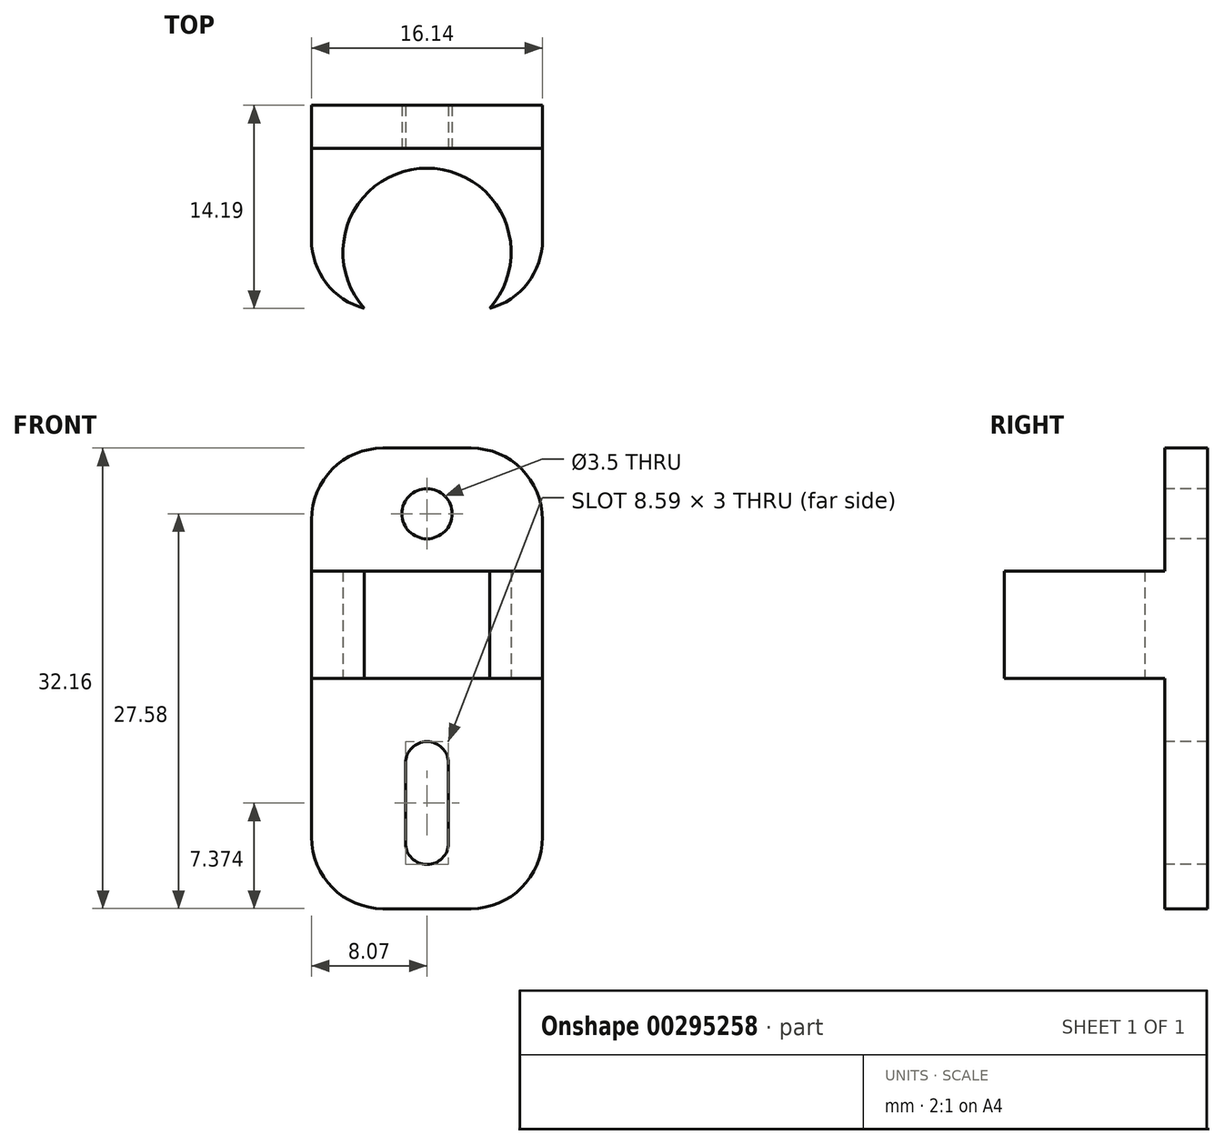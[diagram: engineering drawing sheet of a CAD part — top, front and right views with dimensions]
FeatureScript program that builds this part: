
annotation { "Feature Type Name" : "Feature", "Feature Type Description" : "" }
export const myFeature = defineFeature(function(context is Context, id is Id, definition is map)
    precondition{}
    {
        {
            var Q0;
            Q0=qCreatedBy(makeId("Top.planeOp"),FACE);
            var sketch = newSketch(context, id + "F0", { "sketchPlane" : qUnion([Q0])});
            skArc(sketch, "E0", {"start": v(4.37, -3.93) * mm, "mid": v(0, 5.88) * mm, "end": v(-4.37, -3.93) * mm});
            skLineSegment(sketch, "E1.bottom", {"start": v(8.07, 7.26) * mm, "end": v(-8.07, 7.26) * mm});
            skLineSegment(sketch, "E1.left", {"start": v(8.07, 7.26) * mm, "end": v(8.07, -7.26) * mm});
            skLineSegment(sketch, "E1.right", {"start": v(-8.07, 7.26) * mm, "end": v(-8.07, -7.26) * mm});
            skLineSegment(sketch, "E2", {"start": v(-4.37, -3.93) * mm, "end": v(-8.07, -7.26) * mm});
            skLineSegment(sketch, "E3", {"start": v(4.37, -3.93) * mm, "end": v(8.07, -7.26) * mm});
            skSolve(sketch);
        }
        {
            var Q0;
            Q0 = qSketchRegion(id + "F0", true);
            extrude(context, id + "F1", {"entities" : qUnion([Q0]), "depth" : 7.5 * mm});
        }
        {
            var Q0;
            Q0=makeQuery(id+"F1.opExtrude","SWEPT_FACE",FACE,{"disambiguationData":[OSD([sQuery(id+"F0.wireOp",EDGE,"E1.bottom")])]});
            var sketch = newSketch(context, id + "F2", { "sketchPlane" : qUnion([Q0])});
            skLineSegment(sketch, "E4.bottom", {"start": v(8.07, 0) * mm, "end": v(-8.07, 0) * mm});
            skLineSegment(sketch, "E4.top", {"start": v(8.07, 16.08) * mm, "end": v(-8.07, 16.08) * mm});
            skLineSegment(sketch, "E4.left", {"start": v(8.07, 0) * mm, "end": v(8.07, 16.08) * mm});
            skLineSegment(sketch, "E4.right", {"start": v(-8.07, 0) * mm, "end": v(-8.07, 16.08) * mm});
            skPoint(sketch, "E5", {"position": v(0, 11.5) * mm});
            skPoint(sketch, "E6.MirrorP", {"position": v(0, -11.5) * mm});
            skLineSegment(sketch, "E7.MirrorCS", {"start": v(-8.07, 0) * mm, "end": v(-8.07, -16.08) * mm});
            skLineSegment(sketch, "E8.MirrorCS", {"start": v(8.07, -16.08) * mm, "end": v(-8.07, -16.08) * mm});
            skLineSegment(sketch, "E9.MirrorCS", {"start": v(8.07, 0) * mm, "end": v(8.07, -16.08) * mm});
            skLineSegment(sketch, "E10", {"start": v(0, -11.5) * mm, "end": v(0, -5.91) * mm});
            skArc(sketch, "E11.0.startCap", {"start": v(1.5, -11.5) * mm, "mid": v(0, -13) * mm, "end": v(-1.5, -11.5) * mm});
            skArc(sketch, "E11.0.endCap", {"start": v(-1.5, -5.91) * mm, "mid": v(0, -4.41) * mm, "end": v(1.5, -5.91) * mm});
            skLineSegment(sketch, "E11.0.left", {"start": v(-1.5, -11.5) * mm, "end": v(-1.5, -5.91) * mm});
            skLineSegment(sketch, "E11.0.right", {"start": v(1.5, -11.5) * mm, "end": v(1.5, -5.91) * mm});
            skSolve(sketch);
        }
        {
            var Q0;
            Q0 = qSketchRegion(id + "F2", true);
            extrude(context, id + "F3", {"entities" : qUnion([Q0]), "operationType" : NewBodyOperationType.ADD, "depth" : 3 * mm});
        }
        {
            var Q0;
            Q0=sQuery(id+"F2.wireOp",VERTEX,"E5");
            var Q1;
            Q1=makeQuery(id+"F1.opExtrude","SWEPT_BODY",BODY,{"disambiguationData":[OSD([sQuery(id+"F0.wireOp",EDGE,"E0"),sQuery(id+"F0.wireOp",EDGE,"E1.bottom"),sQuery(id+"F0.wireOp",EDGE,"E1.left"),sQuery(id+"F0.wireOp",EDGE,"E1.right"),sQuery(id+"F0.wireOp",EDGE,"E2"),sQuery(id+"F0.wireOp",EDGE,"E3")])]});
            hole(context, id + "F4", {"style" : HoleStyle.SIMPLE, "endStyle" : HoleEndStyle.THROUGH, "oppositeDirection" : true, "holeDiameter" : 3.5 * mm, "tappedDepth" : 12 * mm, "tapClearance" : 3, "startFromSketch" : true, "locations" : qUnion([Q0]), "scope" : qUnion([Q1])});
        }
        {
            var Q0;
            Q0=makeQuery(id+"F1.opExtrude","SWEPT_EDGE",EDGE,{"disambiguationData":[OSD([sQuery(id+"F0.wireOp",EDGE,"E1.right"),sQuery(id+"F0.wireOp",EDGE,"E2")])]});
            var Q1;
            Q1=makeQuery(id+"F1.opExtrude","SWEPT_EDGE",EDGE,{"disambiguationData":[OSD([sQuery(id+"F0.wireOp",EDGE,"E1.left"),sQuery(id+"F0.wireOp",EDGE,"E3")])]});
            fillet(context, id + "F5", {"entities" : qUnion([Q0, Q1]), "radius" : 5 * mm, "tangentPropagation" : true, "allowEdgeOverflow" : false});
        }
        {
            var Q0;
            Q0=makeQuery(id+"F3.opExtrude","SWEPT_EDGE",EDGE,{"disambiguationData":[OSD([sQuery(id+"F2.wireOp",EDGE,"E4.top"),sQuery(id+"F2.wireOp",EDGE,"E4.left")])]});
            var Q1;
            Q1=makeQuery(id+"F3.opExtrude","SWEPT_EDGE",EDGE,{"disambiguationData":[OSD([sQuery(id+"F2.wireOp",EDGE,"E4.top"),sQuery(id+"F2.wireOp",EDGE,"E4.right")])]});
            var Q2;
            Q2=makeQuery(id+"F3.opExtrude","SWEPT_EDGE",EDGE,{"disambiguationData":[OSD([sQuery(id+"F2.wireOp",EDGE,"E7.MirrorCS"),sQuery(id+"F2.wireOp",EDGE,"E8.MirrorCS")])]});
            var Q3;
            Q3=makeQuery(id+"F3.opExtrude","SWEPT_EDGE",EDGE,{"disambiguationData":[OSD([sQuery(id+"F2.wireOp",EDGE,"E8.MirrorCS"),sQuery(id+"F2.wireOp",EDGE,"E9.MirrorCS")])]});
            fillet(context, id + "F6", {"entities" : qUnion([Q0, Q1, Q2, Q3]), "radius" : 5 * mm, "tangentPropagation" : true, "allowEdgeOverflow" : false});
        }
    });
